# Revit family: Door-NanaWall-NW-Clad-740
name_source: partatom
category: Doors
units: mm (PartAtom-declared; Revit-internal decimal feet)

## family parameters
Always vertical = Yes
Cut with Voids When Loaded = No
Host = Wall
OmniClass Number = 23.30.10.17.17
OmniClass Title = Folding Doors and Grilles
Room Calculation Point = No
Shared = No

## types (5) — shared parameters
04 CSI = 08 41 13
95 CSI = 8411
Analytic Construction = <None>
Assembly Code = B2050.4010
Cost Info = https://www.nanawall.com
Description = Standard Thermally Broken Wood Framed Folding system
Disclaimer = Please note that the Revit model is for schematic purposes only.  To obtain a detailed 3D model, please go to the NanaWall's configurator at www.nanawall.com.
Engineering Details URL = https://www.nanawall.com
Exterior Wall Offset = 5"
Filler = Rubber - NanaWall - Black
Glass Material = Glass - NanaWall - Generic
Installation and Service URL = http://www.nanawall.com
Manufacturer = NanaWall Systems, Inc.
Manufacturer Fax = (415) 383-0312
Model = NW Clad 740
Performance URL = https://www.nanawall.com
Product Page URL = https://www.nanawall.com
Sills Available = Raised, Low Profile Saddle, Flush
Subcategory = Folding Door
Thickness = 3 9/16"
U Value = 0.27
URL = http://www.nanawall.com
Wall Closure = By host
Warranty URL = http://www.nanawall.com

## per-type parameters (varying)
| type | Cladding | Sash |
| Mahogany | Metal - NanaWall - Aluminum | Wood - NanaWall - Mahogany |
| Pine | <By Category> | Wood - NanaWall - Pine |
| Spruce | <By Category> | Wood - NanaWall - Spruce |
| Meranti | <By Category> | Wood - NanaWall - Meranti |
| Western Hemlock | <By Category> | Wood - NanaWall - Western Hemlock |

## geometry (parser evidence)
native form markers: Sweep x20
no freeform markers — native parametric forms only
